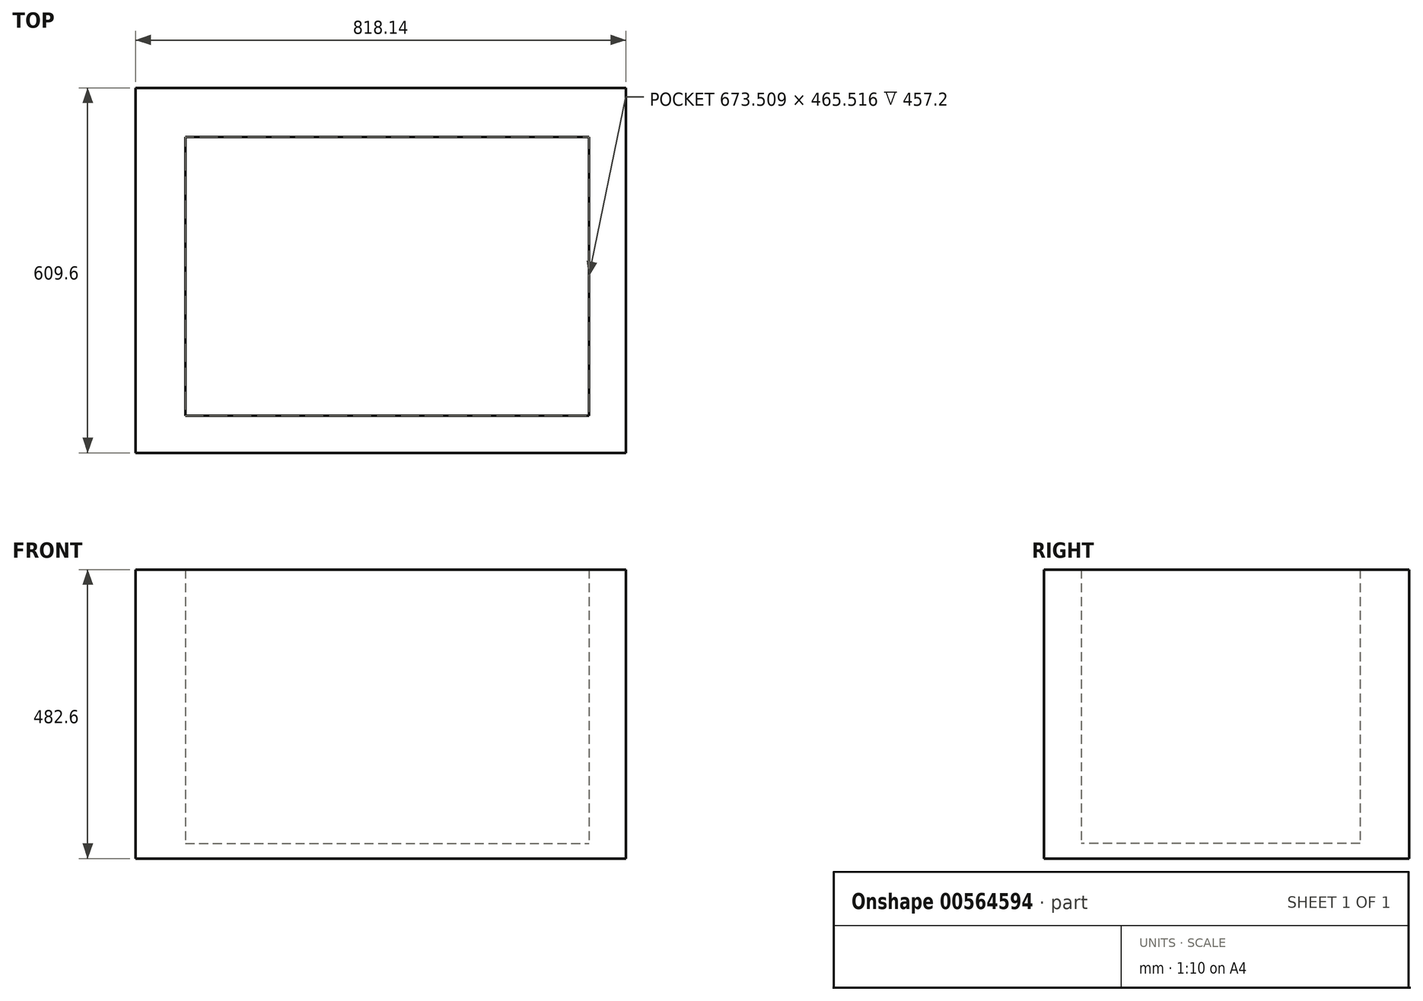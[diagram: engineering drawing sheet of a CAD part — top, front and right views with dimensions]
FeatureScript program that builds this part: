
annotation { "Feature Type Name" : "Feature", "Feature Type Description" : "" }
export const myFeature = defineFeature(function(context is Context, id is Id, definition is map)
    precondition{}
    {
        {
            var Q0;
            Q0=qCreatedBy(makeId("Top.planeOp"),FACE);
            var sketch = newSketch(context, id + "F0", { "sketchPlane" : qUnion([Q0])});
            skLineSegment(sketch, "E0.bottom", {"start": v(398.46, -294.77) * mm, "end": v(-419.68, -294.77) * mm});
            skLineSegment(sketch, "E0.top", {"start": v(398.46, 314.83) * mm, "end": v(-419.68, 314.83) * mm});
            skLineSegment(sketch, "E0.left", {"start": v(398.46, -294.77) * mm, "end": v(398.46, 314.83) * mm});
            skLineSegment(sketch, "E0.right", {"start": v(-419.68, -294.77) * mm, "end": v(-419.68, 314.83) * mm});
            skPoint(sketch, "E0.middle", {"position": v(-10.61, 10.03) * mm});
            skLineSegment(sketch, "E1", {"start": v(-419.68, 314.83) * mm, "end": v(398.46, -294.77) * mm});
            skSolve(sketch);
        }
        {
            var Q0;
            Q0 = qSketchRegion(id + "F0", true);
            extrude(context, id + "F1", {"entities" : qUnion([Q0]), "depth" : 25.4 * mm, "offsetDistance" : 25.4 * mm});
        }
        {
            var Q0;
            Q0=makeQuery(id+"F1.opExtrude","CAP_FACE",FACE,{"disambiguationData":[OSD([sQuery(id+"F0.wireOp",EDGE,"E0.bottom"),sQuery(id+"F0.wireOp",EDGE,"E0.top"),sQuery(id+"F0.wireOp",EDGE,"E0.left"),sQuery(id+"F0.wireOp",EDGE,"E0.right")])],"isStart":false});
            var sketch = newSketch(context, id + "F2", { "sketchPlane" : qUnion([Q0])});
            skLineSegment(sketch, "E2.bottom", {"start": v(-336.75, 232.76) * mm, "end": v(336.75, 232.76) * mm});
            skLineSegment(sketch, "E2.top", {"start": v(-336.75, -232.76) * mm, "end": v(336.75, -232.76) * mm});
            skLineSegment(sketch, "E2.left", {"start": v(-336.75, 232.76) * mm, "end": v(-336.75, -232.76) * mm});
            skLineSegment(sketch, "E2.right", {"start": v(336.75, 232.76) * mm, "end": v(336.75, -232.76) * mm});
            skPoint(sketch, "E2.middle", {"position": v(0, 0) * mm});
            skSolve(sketch);
        }
        {
            var Q0;
            Q0=makeQuery(id+"F2.imprint","IMPRINT",FACE,{"disambiguationData":[TD([[makeQuery(id+"F2.imprint","IMPRINT",EDGE,{"derivedFrom":sQuery(id+"F2.wireOp",EDGE,"E2.bottom")}),1.0]])]});
            extrude(context, id + "F3", {"entities" : qUnion([Q0]), "operationType" : NewBodyOperationType.ADD, "depth" : 457.2 * mm, "offsetDistance" : 25.4 * mm});
        }
    });
